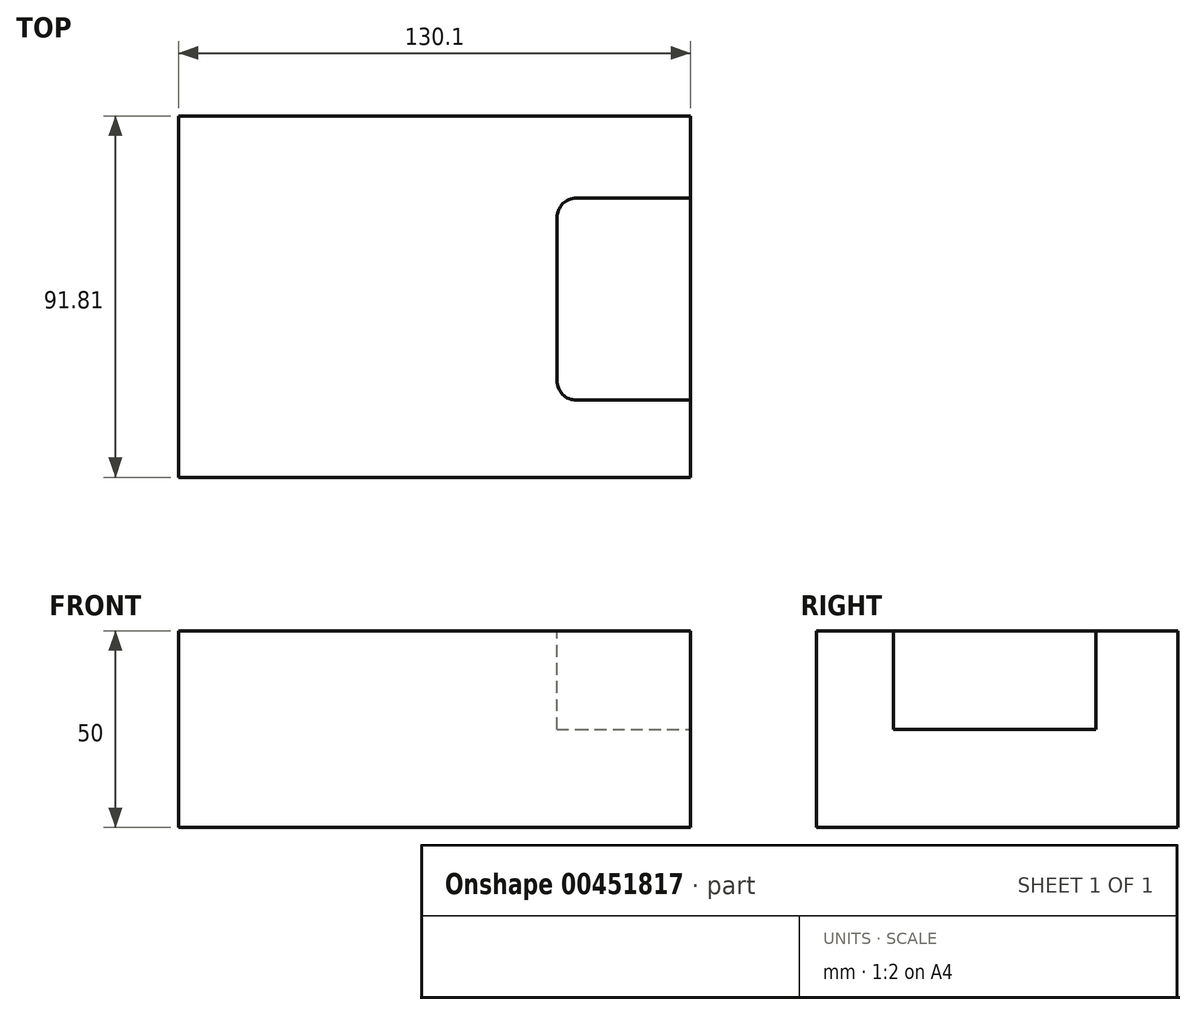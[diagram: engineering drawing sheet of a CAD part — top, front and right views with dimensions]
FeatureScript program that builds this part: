
annotation { "Feature Type Name" : "Feature", "Feature Type Description" : "" }
export const myFeature = defineFeature(function(context is Context, id is Id, definition is map)
    precondition{}
    {
        {
            var Q0;
            Q0=qCreatedBy(makeId("Top.planeOp"),FACE);
            var sketch = newSketch(context, id + "F0", { "sketchPlane" : qUnion([Q0])});
            skLineSegment(sketch, "E0.bottom", {"start": v(-65.32, 47.72) * mm, "end": v(64.78, 47.72) * mm});
            skLineSegment(sketch, "E0.top", {"start": v(-65.32, -44.1) * mm, "end": v(64.78, -44.1) * mm});
            skLineSegment(sketch, "E0.left", {"start": v(-65.32, 47.72) * mm, "end": v(-65.32, -44.1) * mm});
            skLineSegment(sketch, "E0.right", {"start": v(64.78, 47.72) * mm, "end": v(64.78, -44.1) * mm});
            skSolve(sketch);
        }
        {
            var Q0;
            Q0=makeQuery(id+"F0.imprint","IMPRINT",FACE,{"disambiguationData":[TD([[makeQuery(id+"F0.imprint","IMPRINT",EDGE,{"derivedFrom":sQuery(id+"F0.wireOp",EDGE,"E0.bottom")}),-1.0]])]});
            extrude(context, id + "F1", {"entities" : qUnion([Q0]), "depth" : 50 * mm});
        }
        {
            var Q0;
            Q0=makeQuery(id+"F1.opExtrude","CAP_FACE",FACE,{"disambiguationData":[OSD([sQuery(id+"F0.wireOp",EDGE,"E0.bottom"),sQuery(id+"F0.wireOp",EDGE,"E0.top"),sQuery(id+"F0.wireOp",EDGE,"E0.left"),sQuery(id+"F0.wireOp",EDGE,"E0.right")])],"isStart":false});
            var sketch = newSketch(context, id + "F2", { "sketchPlane" : qUnion([Q0])});
            skLineSegment(sketch, "E1.bottom", {"start": v(30.85, 26.85) * mm, "end": v(94.54, 26.85) * mm});
            skLineSegment(sketch, "E1.top", {"start": v(30.85, -24.5) * mm, "end": v(94.54, -24.5) * mm});
            skLineSegment(sketch, "E1.left", {"start": v(30.85, 26.85) * mm, "end": v(30.85, -24.5) * mm});
            skLineSegment(sketch, "E1.right", {"start": v(94.54, 26.85) * mm, "end": v(94.54, -24.5) * mm});
            skSolve(sketch);
        }
        {
            var Q0;
            {var subQ0=sQuery(id+"F2.wireOp",EDGE,"E1.left");Q0=makeQuery(id+"F2.imprint","IMPRINT",FACE,{"disambiguationData":[TD([[makeQuery(id+"F2.imprint","IMPRINT",EDGE,{"derivedFrom":subQ0}),1.0]])]});}
            extrude(context, id + "F3", {"entities" : qUnion([Q0]), "operationType" : NewBodyOperationType.REMOVE, "oppositeDirection" : true, "depth" : 25 * mm});
        }
        {
            var Q0;
            Q0=makeQuery(id+"F3.boolean.opBoolean","COPY",EDGE,{"derivedFrom":makeQuery(id+"F3.opExtrude","SWEPT_EDGE",EDGE,{"disambiguationData":[OSD([sQuery(id+"F2.wireOp",EDGE,"E1.bottom"),sQuery(id+"F2.wireOp",EDGE,"E1.left")])]})});
            var Q1;
            Q1=makeQuery(id+"F3.boolean.opBoolean","COPY",EDGE,{"derivedFrom":makeQuery(id+"F3.opExtrude","SWEPT_EDGE",EDGE,{"disambiguationData":[OSD([sQuery(id+"F2.wireOp",EDGE,"E1.top"),sQuery(id+"F2.wireOp",EDGE,"E1.left")])]})});
            fillet(context, id + "F4", {"entities" : qUnion([Q0, Q1]), "radius" : 5 * mm, "tangentPropagation" : true, "allowEdgeOverflow" : false});
        }
    });
